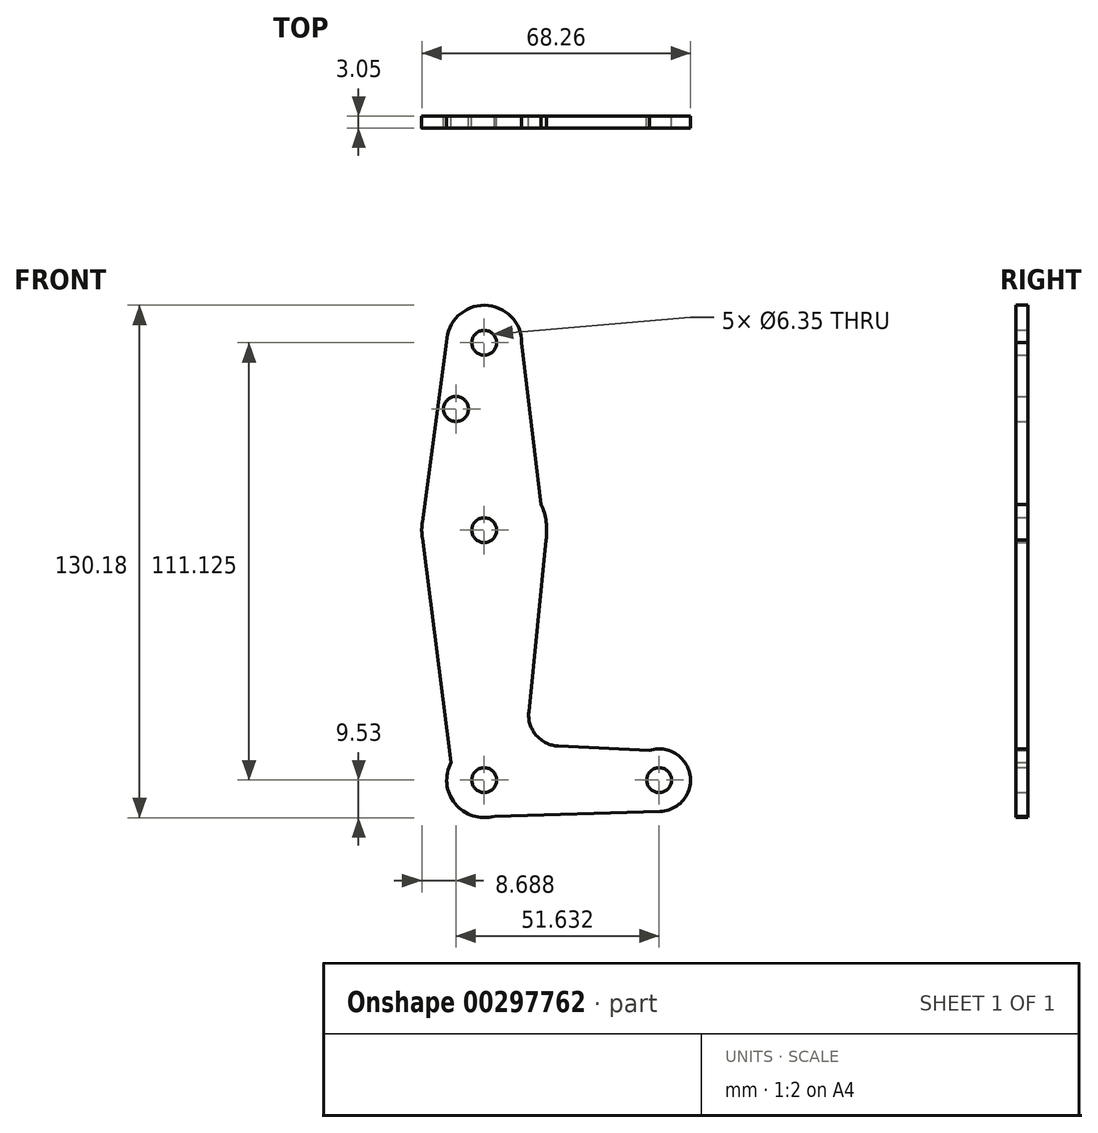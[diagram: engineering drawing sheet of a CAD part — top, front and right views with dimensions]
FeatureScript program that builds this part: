
annotation { "Feature Type Name" : "Feature", "Feature Type Description" : "" }
export const myFeature = defineFeature(function(context is Context, id is Id, definition is map)
    precondition{}
    {
        {
            var Q0;
            Q0=qCreatedBy(makeId("Front.planeOp"),FACE);
            var sketch = newSketch(context, id + "F0", { "sketchPlane" : qUnion([Q0])});
            skCircle(sketch, "E0", {"center": v(0, 0) * mm, "radius": 9.52 * mm});
            skCircle(sketch, "E1", {"center": v(44.45, 0) * mm, "radius": 7.94 * mm});
            skCircle(sketch, "E2", {"center": v(0, 63.5) * mm, "radius": 15.88 * mm});
            skCircle(sketch, "E3", {"center": v(0, 111.12) * mm, "radius": 9.52 * mm});
            skLineSegment(sketch, "E4", {"start": v(0, 0) * mm, "end": v(44.45, 0) * mm, "construction": true});
            skLineSegment(sketch, "E5", {"start": v(0, 63.5) * mm, "end": v(0, 0) * mm, "construction": true});
            skPoint(sketch, "E6.endSnap0", {"position": v(22.23, 0) * mm});
            skCircle(sketch, "E7", {"center": v(0, 111.12) * mm, "radius": 3.18 * mm});
            skCircle(sketch, "E8", {"center": v(0, 63.5) * mm, "radius": 3.18 * mm});
            skCircle(sketch, "E9", {"center": v(0, 0) * mm, "radius": 3.18 * mm});
            skCircle(sketch, "E10", {"center": v(44.45, 0) * mm, "radius": 3.18 * mm});
            skPoint(sketch, "E11.newPointA", {"position": v(9.53, 0) * mm});
            skLineSegment(sketch, "E12", {"start": v(0, 111.12) * mm, "end": v(0, -3.17) * mm, "construction": true});
            skCircle(sketch, "E13", {"center": v(-7.18, 94.3) * mm, "radius": 3.18 * mm});
            skLineSegment(sketch, "E14", {"start": v(-9.52, 111.36) * mm, "end": v(-15.73, 65.64) * mm});
            skLineSegment(sketch, "E15", {"start": v(-15.74, 61.46) * mm, "end": v(-8.38, 4.53) * mm});
            skLineSegment(sketch, "E16", {"start": v(9.53, 111.12) * mm, "end": v(14.45, 70.08) * mm});
            skLineSegment(sketch, "E17", {"start": v(15.68, 61.01) * mm, "end": v(11.31, 17.38) * mm});
            skLineSegment(sketch, "E18", {"start": v(2.6, -9.17) * mm, "end": v(44.68, -7.93) * mm});
            skLineSegment(sketch, "E19", {"start": v(42, 7.55) * mm, "end": v(18.85, 8.64) * mm});
            skPoint(sketch, "E20.newPointA", {"position": v(10.03, 4.53) * mm});
            skArc(sketch, "E20.filletArc", {"start": v(11.31, 17.38) * mm, "mid": v(13.2, 11.4) * mm, "end": v(18.85, 8.64) * mm});
            skSolve(sketch);
        }
        {
            var Q0;
            Q0 = qSketchRegion(id + "F0", true);
            extrude(context, id + "F1", {"entities" : qUnion([Q0]), "depth" : 3.05 * mm});
        }
    });
